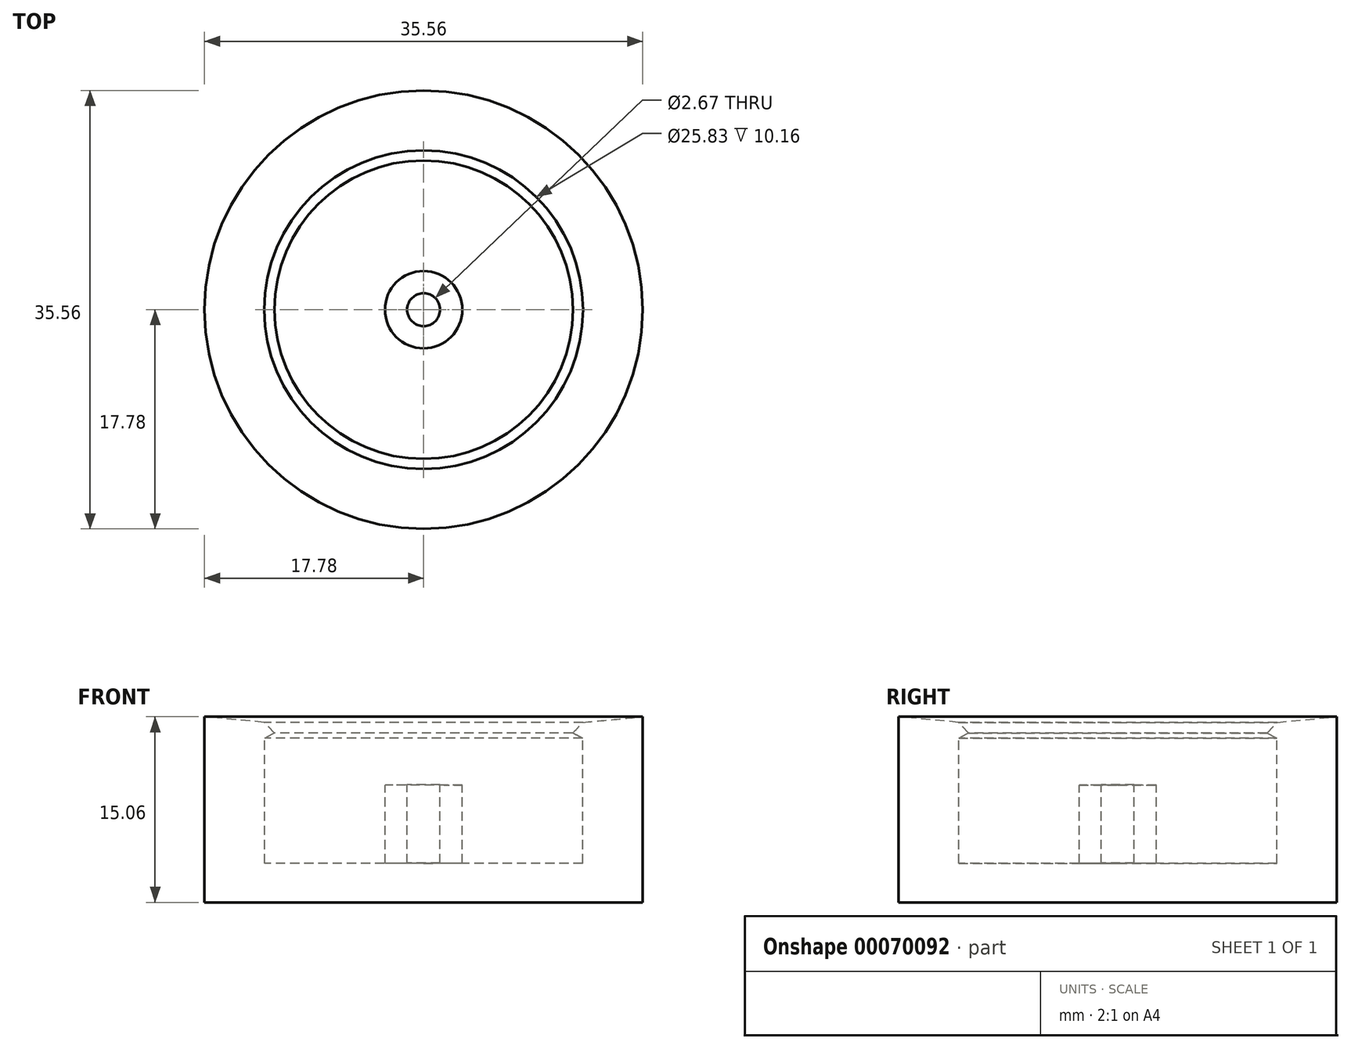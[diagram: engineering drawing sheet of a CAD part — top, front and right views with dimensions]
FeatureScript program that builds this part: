
annotation { "Feature Type Name" : "Feature", "Feature Type Description" : "" }
export const myFeature = defineFeature(function(context is Context, id is Id, definition is map)
    precondition{}
    {
        {
            var Q0;
            Q0=qCreatedBy(makeId("Front.planeOp"),FACE);
            var sketch = newSketch(context, id + "F0", { "sketchPlane" : qUnion([Q0])});
            skLineSegment(sketch, "E0", {"start": v(-17.78, 13.34) * mm, "end": v(-17.78, 0) * mm});
            skLineSegment(sketch, "E1", {"start": v(-17.78, 0) * mm, "end": v(0, 0) * mm});
            skLineSegment(sketch, "E2", {"start": v(-3.14, 9.52) * mm, "end": v(-3.14, 3.17) * mm});
            skLineSegment(sketch, "E3", {"start": v(-3.14, 3.17) * mm, "end": v(-12.92, 3.17) * mm});
            skLineSegment(sketch, "E4", {"start": v(-12.92, 3.17) * mm, "end": v(-12.92, 13.33) * mm});
            skLineSegment(sketch, "E5", {"start": v(-1.33, 3.18) * mm, "end": v(0, 3.18) * mm});
            skLineSegment(sketch, "E6", {"start": v(0, 3.18) * mm, "end": v(0, 0) * mm});
            skLineSegment(sketch, "E7", {"start": v(-1.33, 9.53) * mm, "end": v(-1.33, 3.18) * mm});
            skLineSegment(sketch, "E8", {"start": v(-1.33, 9.53) * mm, "end": v(-3.14, 9.52) * mm});
            skLineSegment(sketch, "E9", {"start": v(-12.92, 13.33) * mm, "end": v(-12.1, 13.74) * mm});
            skLineSegment(sketch, "E10", {"start": v(-12.1, 13.74) * mm, "end": v(-12.93, 14.6) * mm});
            skLineSegment(sketch, "E11", {"start": v(-12.93, 14.6) * mm, "end": v(-17.78, 15.06) * mm});
            skLineSegment(sketch, "E12", {"start": v(-17.78, 15.06) * mm, "end": v(-17.78, 13.34) * mm});
            skSolve(sketch);
        }
        {
            var Q0;
            Q0=qCreatedBy(makeId("Top.planeOp"),FACE);
            var sketch = newSketch(context, id + "F1", { "sketchPlane" : qUnion([Q0])});
            skCircle(sketch, "E13", {"center": v(0, 0) * mm, "radius": 1.34 * mm});
            skSolve(sketch);
        }
        {
            var Q0;
            Q0=sQuery(id+"F1.wireOp",EDGE,"E13");
            extrude(context, id + "F2", {"bodyType" : ToolBodyType.SURFACE, "surfaceEntities" : qUnion([Q0]), "depth" : 11 * mm});
        }
        {
            var Q0;
            Q0=makeQuery(id+"F0.imprint","IMPRINT",FACE,{"disambiguationData":[TD([[makeQuery(id+"F0.imprint","IMPRINT",EDGE,{"derivedFrom":sQuery(id+"F0.wireOp",EDGE,"E0")}),1.0]])]});
            var Q1;
            Q1=sQuery(id+"F0.wireOp",EDGE,"E6");
            revolve(context, id + "F3", {"entities" : qUnion([Q0]), "axis" : qUnion([Q1]), "revolveType" : RevolveType.FULL});
        }
    });
